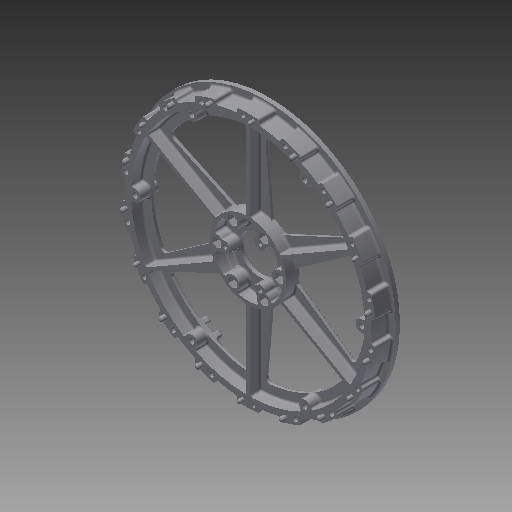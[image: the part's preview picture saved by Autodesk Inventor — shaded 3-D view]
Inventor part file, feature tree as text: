
AUTODESK INVENTOR PART (.ipt)
format: ipt  version: 2018 (Build 220112000, 112)  size: 3,231,232 bytes
history: native  units: in
note: dims shown in document units (in); Inventor stores cm internally (conversion verified against a paired STEP export)
features: chamfer x1, other x1, imported_body x1
ambient origin geometry x8: Origin, YZ Plane, XZ Plane, XY Plane, X Axis, Y Axis, Z Axis, Center Point
bodies: Body1 (feature_tree)
feature tree (3):
  chamfer  "Chamfer1"  [1 undecoded]
  other  "217-2605-001 Rev1.ipt1"
  imported_body  "Base1"
note: 1 required parameter value undecoded (feature->parameter linkage not recoverable at this tier; creation-order binding heuristic only, values carry confidence <= 0.55)
